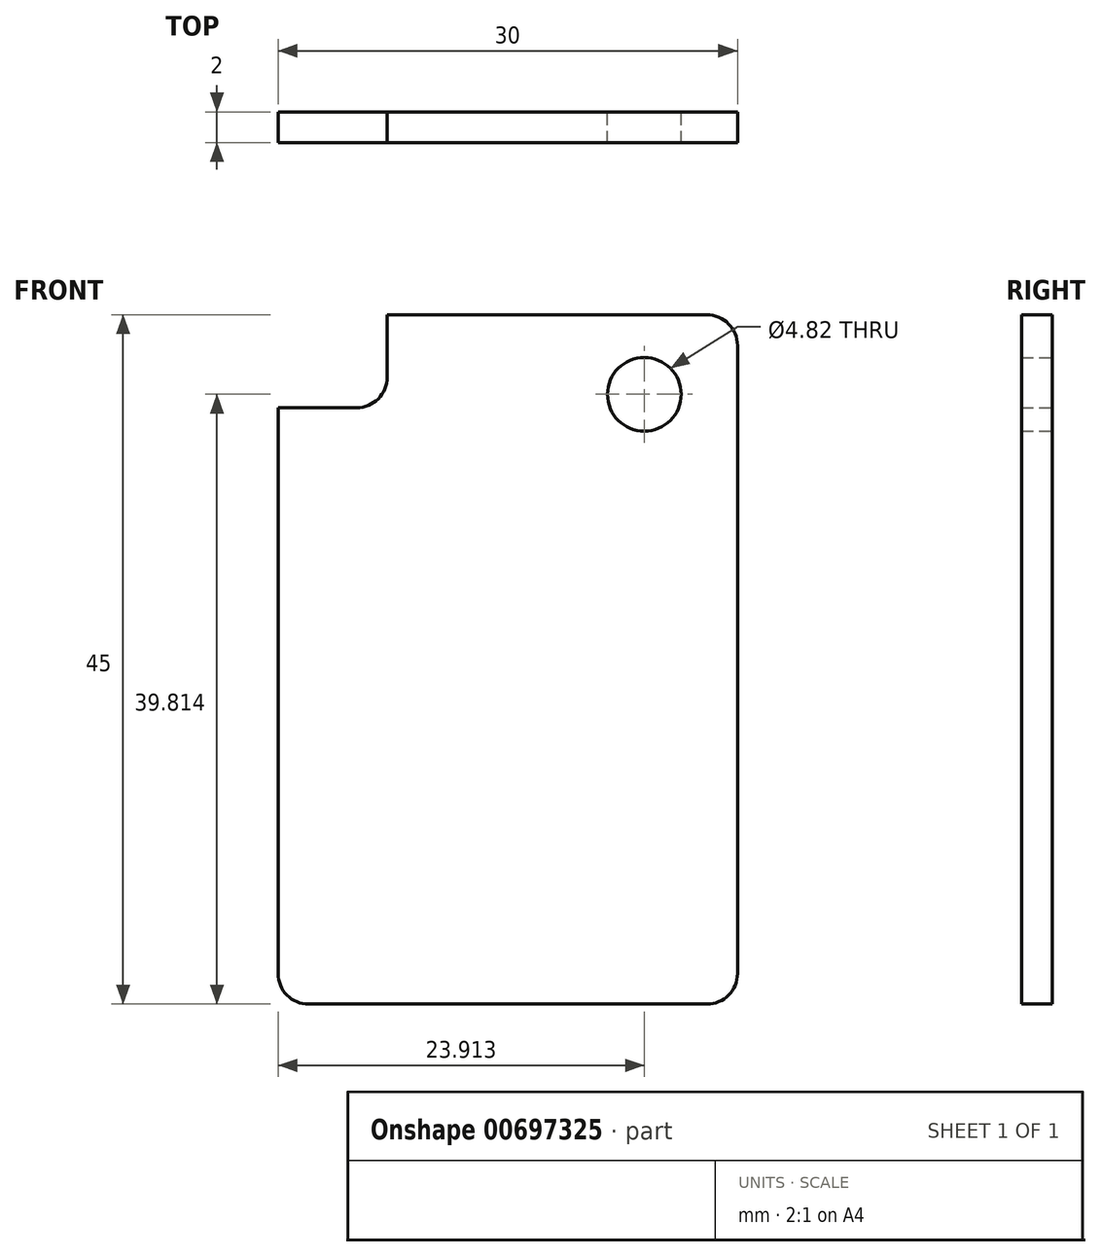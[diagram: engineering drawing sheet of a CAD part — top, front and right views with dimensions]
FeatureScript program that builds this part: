
annotation { "Feature Type Name" : "Feature", "Feature Type Description" : "" }
export const myFeature = defineFeature(function(context is Context, id is Id, definition is map)
    precondition{}
    {
        {
            var Q0;
            Q0=qCreatedBy(makeId("Front.planeOp"),FACE);
            var sketch = newSketch(context, id + "F0", { "sketchPlane" : qUnion([Q0])});
            skLineSegment(sketch, "E0.bottom", {"start": v(8.99, 11.44) * mm, "end": v(38.99, 11.44) * mm});
            skLineSegment(sketch, "E0.top", {"start": v(8.99, 56.44) * mm, "end": v(38.99, 56.44) * mm});
            skLineSegment(sketch, "E0.left", {"start": v(8.99, 11.44) * mm, "end": v(8.99, 56.44) * mm});
            skLineSegment(sketch, "E0.right", {"start": v(38.99, 11.44) * mm, "end": v(38.99, 56.44) * mm});
            skSolve(sketch);
        }
        {
            var Q0;
            Q0 = qSketchRegion(id + "F0", true);
            extrude(context, id + "F1", {"entities" : qUnion([Q0]), "depth" : 2 * mm, "offsetDistance" : 25 * mm});
        }
        {
            var Q0;
            Q0=qCreatedBy(makeId("Front.planeOp"),FACE);
            var sketch = newSketch(context, id + "F2", { "sketchPlane" : qUnion([Q0])});
            skLineSegment(sketch, "E1.bottom", {"start": v(8.99, 50.38) * mm, "end": v(16.12, 50.38) * mm});
            skLineSegment(sketch, "E1.top", {"start": v(8.99, 56.44) * mm, "end": v(16.12, 56.44) * mm});
            skLineSegment(sketch, "E1.left", {"start": v(8.99, 50.38) * mm, "end": v(8.99, 56.44) * mm});
            skLineSegment(sketch, "E1.right", {"start": v(16.12, 50.38) * mm, "end": v(16.12, 56.44) * mm});
            skCircle(sketch, "E2", {"center": v(32.9, 51.25) * mm, "radius": 2.4 * mm});
            skSolve(sketch);
        }
        {
            var Q0;
            Q0 = qSketchRegion(id + "F2", true);
            extrude(context, id + "F3", {"entities" : qUnion([Q0]), "operationType" : NewBodyOperationType.REMOVE, "endBound" : BoundingType.THROUGH_ALL, "depth" : 25 * mm, "offsetDistance" : 25 * mm});
        }
        {
            var Q0;
            Q0=makeQuery(id+"F3.boolean.opBoolean","COPY",EDGE,{"derivedFrom":makeQuery(id+"F3.opExtrude","SWEPT_EDGE",EDGE,{"disambiguationData":[OSD([sQuery(id+"F2.wireOp",EDGE,"E1.bottom"),sQuery(id+"F2.wireOp",EDGE,"E1.left")])]})});
            var Q1;
            Q1=makeQuery(id+"F3.boolean.opBoolean","COPY",EDGE,{"derivedFrom":makeQuery(id+"F3.opExtrude","SWEPT_EDGE",EDGE,{"disambiguationData":[OSD([sQuery(id+"F2.wireOp",EDGE,"E1.bottom"),sQuery(id+"F2.wireOp",EDGE,"E1.right")])]})});
            var Q2;
            Q2=makeQuery(id+"F3.boolean.opBoolean","COPY",EDGE,{"derivedFrom":makeQuery(id+"F3.opExtrude","SWEPT_EDGE",EDGE,{"disambiguationData":[OSD([sQuery(id+"F2.wireOp",EDGE,"E1.top"),sQuery(id+"F2.wireOp",EDGE,"E1.right")])]})});
            var Q3;
            Q3=makeQuery(id+"F1.opExtrude","SWEPT_EDGE",EDGE,{"disambiguationData":[OSD([sQuery(id+"F0.wireOp",EDGE,"E0.top"),sQuery(id+"F0.wireOp",EDGE,"E0.right")])]});
            var Q4;
            Q4=makeQuery(id+"F1.opExtrude","SWEPT_EDGE",EDGE,{"disambiguationData":[OSD([sQuery(id+"F0.wireOp",EDGE,"E0.bottom"),sQuery(id+"F0.wireOp",EDGE,"E0.right")])]});
            var Q5;
            Q5=makeQuery(id+"F1.opExtrude","SWEPT_EDGE",EDGE,{"disambiguationData":[OSD([sQuery(id+"F0.wireOp",EDGE,"E0.bottom"),sQuery(id+"F0.wireOp",EDGE,"E0.left")])]});
            fillet(context, id + "F4", {"entities" : qUnion([Q0, Q1, Q2, Q3, Q4, Q5]), "radius" : 2 * mm, "tangentPropagation" : true, "allowEdgeOverflow" : false});
        }
    });
